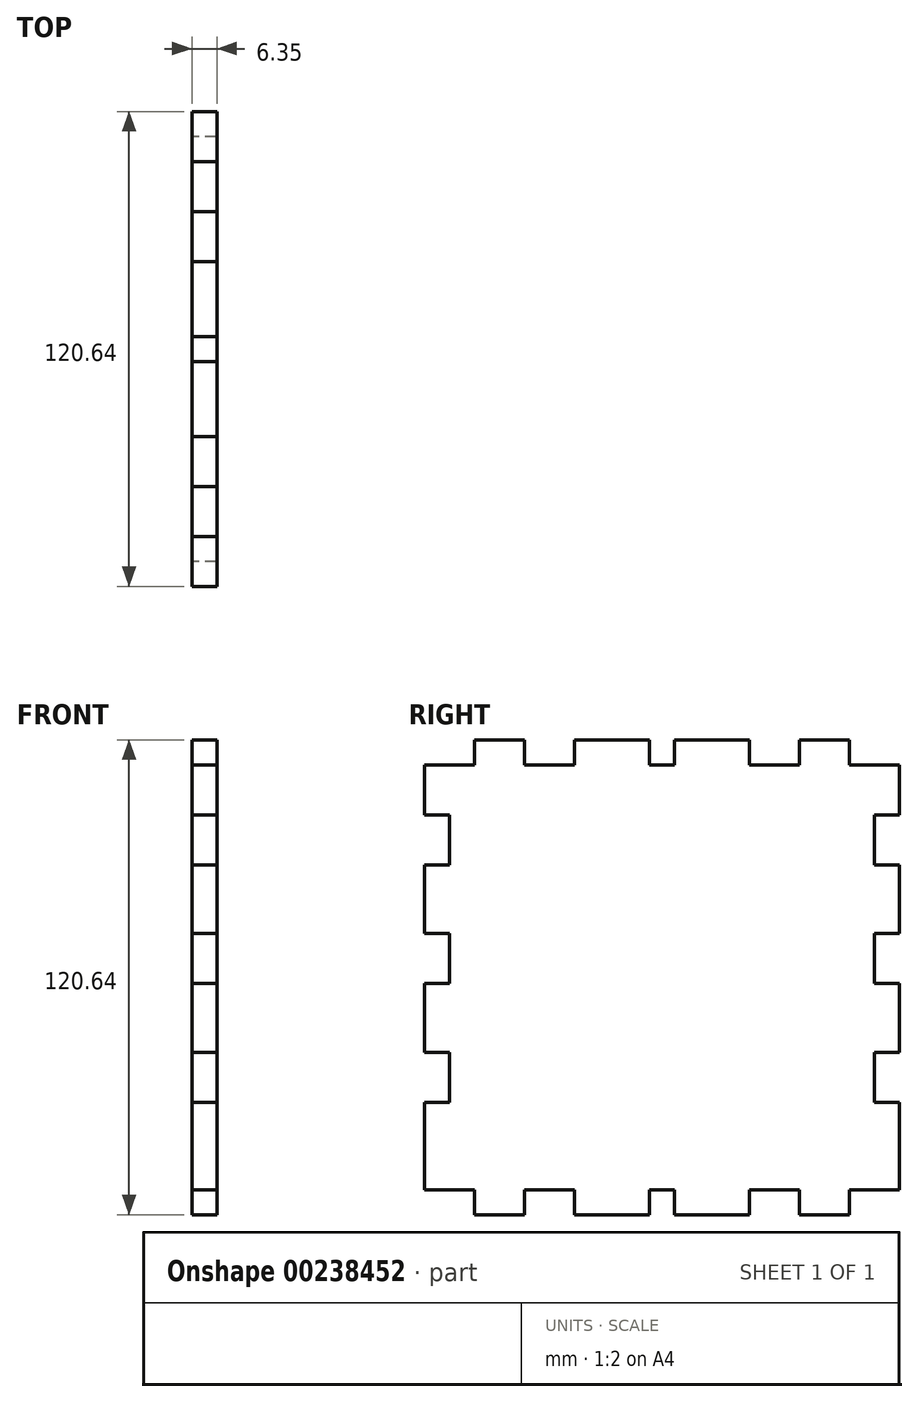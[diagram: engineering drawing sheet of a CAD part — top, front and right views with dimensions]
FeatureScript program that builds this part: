
annotation { "Feature Type Name" : "Feature", "Feature Type Description" : "" }
export const myFeature = defineFeature(function(context is Context, id is Id, definition is map)
    precondition{}
    {
        {
            var Q0;
            Q0=qCreatedBy(makeId("Right.planeOp"),FACE);
            var sketch = newSketch(context, id + "F0", { "sketchPlane" : qUnion([Q0])});
            skLineSegment(sketch, "E0.bottom", {"start": v(60.32, 60.33) * mm, "end": v(-60.33, 60.33) * mm});
            skLineSegment(sketch, "E0.top", {"start": v(60.33, -60.33) * mm, "end": v(-60.32, -60.33) * mm});
            skLineSegment(sketch, "E0.left", {"start": v(60.32, 60.33) * mm, "end": v(60.33, -60.33) * mm});
            skLineSegment(sketch, "E0.right", {"start": v(-60.33, 60.33) * mm, "end": v(-60.32, -60.33) * mm});
            skPoint(sketch, "E0.middle", {"position": v(0, 0) * mm});
            skSolve(sketch);
        }
        {
            var Q0;
            Q0=makeQuery(id+"F0.imprint","IMPRINT",FACE,{"disambiguationData":[TD([[makeQuery(id+"F0.imprint","IMPRINT",EDGE,{"derivedFrom":sQuery(id+"F0.wireOp",EDGE,"E0.bottom")}),1.0]])]});
            extrude(context, id + "F1", {"entities" : qUnion([Q0]), "depth" : 6.35 * mm});
        }
        {
            var Q0;
            Q0=makeQuery(id+"F1.opExtrude","CAP_FACE",FACE,{"disambiguationData":[OSD([sQuery(id+"F0.wireOp",EDGE,"E0.bottom"),sQuery(id+"F0.wireOp",EDGE,"E0.top"),sQuery(id+"F0.wireOp",EDGE,"E0.left"),sQuery(id+"F0.wireOp",EDGE,"E0.right")])],"isStart":true});
            var sketch = newSketch(context, id + "F2", { "sketchPlane" : qUnion([Q0])});
            skLineSegment(sketch, "E1.bottom", {"start": v(60.33, 60.33) * mm, "end": v(47.63, 60.33) * mm});
            skLineSegment(sketch, "E1.top", {"start": v(60.33, 53.98) * mm, "end": v(47.63, 53.98) * mm});
            skLineSegment(sketch, "E1.left", {"start": v(60.33, 60.33) * mm, "end": v(60.33, 53.98) * mm});
            skLineSegment(sketch, "E1.right", {"start": v(47.63, 60.33) * mm, "end": v(47.63, 53.98) * mm});
            skSolve(sketch);
        }
        {
            var Q0;
            Q0=makeQuery(id+"F2.imprint","IMPRINT",FACE,{"disambiguationData":[TD([[makeQuery(id+"F2.imprint","IMPRINT",EDGE,{"derivedFrom":sQuery(id+"F2.wireOp",EDGE,"E1.bottom")}),-1.0]])]});
            extrude(context, id + "F3", {"entities" : qUnion([Q0]), "operationType" : NewBodyOperationType.REMOVE, "endBound" : BoundingType.THROUGH_ALL, "oppositeDirection" : true, "depth" : 1.59 * mm});
        }
        {
            var Q0;
            Q0=makeQuery(id+"F1.opExtrude","CAP_FACE",FACE,{"disambiguationData":[OSD([sQuery(id+"F0.wireOp",EDGE,"E0.bottom"),sQuery(id+"F0.wireOp",EDGE,"E0.top"),sQuery(id+"F0.wireOp",EDGE,"E0.left"),sQuery(id+"F0.wireOp",EDGE,"E0.right")])],"isStart":true});
            var sketch = newSketch(context, id + "F4", { "sketchPlane" : qUnion([Q0])});
            skLineSegment(sketch, "E2.bottom", {"start": v(34.93, 60.33) * mm, "end": v(22.23, 60.33) * mm});
            skLineSegment(sketch, "E2.top", {"start": v(34.93, 53.98) * mm, "end": v(22.23, 53.98) * mm});
            skLineSegment(sketch, "E2.left", {"start": v(34.93, 60.33) * mm, "end": v(34.93, 53.98) * mm});
            skLineSegment(sketch, "E2.right", {"start": v(22.23, 60.33) * mm, "end": v(22.23, 53.98) * mm});
            skSolve(sketch);
        }
        {
            var Q0;
            Q0=qSketchRegion(id+"F4",true);
            extrude(context, id + "F5", {"entities" : qUnion([Q0]), "operationType" : NewBodyOperationType.REMOVE, "endBound" : BoundingType.THROUGH_ALL, "oppositeDirection" : true, "depth" : 1.59 * mm});
        }
        {
            var Q0;
            Q0=makeQuery(id+"F1.opExtrude","CAP_FACE",FACE,{"disambiguationData":[OSD([sQuery(id+"F0.wireOp",EDGE,"E0.bottom"),sQuery(id+"F0.wireOp",EDGE,"E0.top"),sQuery(id+"F0.wireOp",EDGE,"E0.left"),sQuery(id+"F0.wireOp",EDGE,"E0.right")])],"isStart":true});
            var sketch = newSketch(context, id + "F6", { "sketchPlane" : qUnion([Q0])});
            skLineSegment(sketch, "E3.bottom", {"start": v(3.18, 60.33) * mm, "end": v(-3.17, 60.33) * mm});
            skLineSegment(sketch, "E3.top", {"start": v(3.18, 53.98) * mm, "end": v(-3.17, 53.98) * mm});
            skLineSegment(sketch, "E3.left", {"start": v(3.18, 60.33) * mm, "end": v(3.18, 53.98) * mm});
            skLineSegment(sketch, "E3.right", {"start": v(-3.17, 60.33) * mm, "end": v(-3.17, 53.98) * mm});
            skSolve(sketch);
        }
        {
            var Q0;
            Q0=qSketchRegion(id+"F6",true);
            extrude(context, id + "F7", {"entities" : qUnion([Q0]), "operationType" : NewBodyOperationType.REMOVE, "endBound" : BoundingType.THROUGH_ALL, "oppositeDirection" : true, "depth" : 1.59 * mm});
        }
        {
            var Q0;
            Q0=makeQuery(id+"F1.opExtrude","CAP_FACE",FACE,{"disambiguationData":[OSD([sQuery(id+"F0.wireOp",EDGE,"E0.bottom"),sQuery(id+"F0.wireOp",EDGE,"E0.top"),sQuery(id+"F0.wireOp",EDGE,"E0.left"),sQuery(id+"F0.wireOp",EDGE,"E0.right")])],"isStart":true});
            var sketch = newSketch(context, id + "F8", { "sketchPlane" : qUnion([Q0])});
            skLineSegment(sketch, "E4.bottom", {"start": v(-60.32, 60.33) * mm, "end": v(-47.62, 60.33) * mm});
            skLineSegment(sketch, "E4.top", {"start": v(-60.32, 53.98) * mm, "end": v(-47.62, 53.98) * mm});
            skLineSegment(sketch, "E4.left", {"start": v(-60.32, 60.33) * mm, "end": v(-60.32, 53.98) * mm});
            skLineSegment(sketch, "E4.right", {"start": v(-47.62, 60.33) * mm, "end": v(-47.62, 53.98) * mm});
            skSolve(sketch);
        }
        {
            var Q0;
            Q0=makeQuery(id+"F8.imprint","IMPRINT",FACE,{"disambiguationData":[TD([[makeQuery(id+"F8.imprint","IMPRINT",EDGE,{"derivedFrom":sQuery(id+"F8.wireOp",EDGE,"E4.bottom")}),-1.0]])]});
            extrude(context, id + "F9", {"entities" : qUnion([Q0]), "operationType" : NewBodyOperationType.REMOVE, "endBound" : BoundingType.THROUGH_ALL, "oppositeDirection" : true, "depth" : 1.59 * mm});
        }
        {
            var Q0;
            Q0=makeQuery(id+"F1.opExtrude","CAP_FACE",FACE,{"disambiguationData":[OSD([sQuery(id+"F0.wireOp",EDGE,"E0.bottom"),sQuery(id+"F0.wireOp",EDGE,"E0.top"),sQuery(id+"F0.wireOp",EDGE,"E0.left"),sQuery(id+"F0.wireOp",EDGE,"E0.right")])],"isStart":true});
            var sketch = newSketch(context, id + "F10", { "sketchPlane" : qUnion([Q0])});
            skLineSegment(sketch, "E5.bottom", {"start": v(-22.22, 60.33) * mm, "end": v(-34.92, 60.33) * mm});
            skLineSegment(sketch, "E5.top", {"start": v(-22.22, 53.98) * mm, "end": v(-34.92, 53.98) * mm});
            skLineSegment(sketch, "E5.left", {"start": v(-22.22, 60.33) * mm, "end": v(-22.22, 53.98) * mm});
            skLineSegment(sketch, "E5.right", {"start": v(-34.92, 60.33) * mm, "end": v(-34.92, 53.98) * mm});
            skSolve(sketch);
        }
        {
            var Q0;
            Q0=makeQuery(id+"F10.imprint","IMPRINT",FACE,{"disambiguationData":[TD([[makeQuery(id+"F10.imprint","IMPRINT",EDGE,{"derivedFrom":sQuery(id+"F10.wireOp",EDGE,"E5.bottom")}),-1.0]])]});
            extrude(context, id + "F11", {"entities" : qUnion([Q0]), "operationType" : NewBodyOperationType.REMOVE, "endBound" : BoundingType.THROUGH_ALL, "oppositeDirection" : true, "depth" : 1.59 * mm});
        }
        {
            var Q0;
            Q0=makeQuery(id+"F1.opExtrude","CAP_FACE",FACE,{"disambiguationData":[OSD([sQuery(id+"F0.wireOp",EDGE,"E0.bottom"),sQuery(id+"F0.wireOp",EDGE,"E0.top"),sQuery(id+"F0.wireOp",EDGE,"E0.left"),sQuery(id+"F0.wireOp",EDGE,"E0.right")])],"isStart":true});
            var sketch = newSketch(context, id + "F12", { "sketchPlane" : qUnion([Q0])});
            skLineSegment(sketch, "E6.bottom", {"start": v(-60.32, 41.28) * mm, "end": v(-53.97, 41.28) * mm});
            skLineSegment(sketch, "E6.top", {"start": v(-60.32, 28.58) * mm, "end": v(-53.97, 28.58) * mm});
            skLineSegment(sketch, "E6.left", {"start": v(-60.32, 41.28) * mm, "end": v(-60.32, 28.57) * mm});
            skLineSegment(sketch, "E6.right", {"start": v(-53.97, 41.28) * mm, "end": v(-53.97, 28.58) * mm});
            skSolve(sketch);
        }
        {
            var Q0;
            Q0=makeQuery(id+"F12.imprint","IMPRINT",FACE,{"disambiguationData":[TD([[makeQuery(id+"F12.imprint","IMPRINT",EDGE,{"derivedFrom":sQuery(id+"F12.wireOp",EDGE,"E6.bottom")}),-1.0]])]});
            extrude(context, id + "F13", {"entities" : qUnion([Q0]), "operationType" : NewBodyOperationType.REMOVE, "endBound" : BoundingType.THROUGH_ALL, "oppositeDirection" : true, "depth" : 1.59 * mm});
        }
        {
            var Q0;
            Q0=makeQuery(id+"F1.opExtrude","CAP_FACE",FACE,{"disambiguationData":[OSD([sQuery(id+"F0.wireOp",EDGE,"E0.bottom"),sQuery(id+"F0.wireOp",EDGE,"E0.top"),sQuery(id+"F0.wireOp",EDGE,"E0.left"),sQuery(id+"F0.wireOp",EDGE,"E0.right")])],"isStart":true});
            var sketch = newSketch(context, id + "F14", { "sketchPlane" : qUnion([Q0])});
            skLineSegment(sketch, "E7.bottom", {"start": v(-60.32, 11.11) * mm, "end": v(-53.97, 11.11) * mm});
            skLineSegment(sketch, "E7.top", {"start": v(-60.32, -1.59) * mm, "end": v(-53.97, -1.59) * mm});
            skLineSegment(sketch, "E7.left", {"start": v(-60.32, 11.11) * mm, "end": v(-60.32, -1.59) * mm});
            skLineSegment(sketch, "E7.right", {"start": v(-53.97, 11.11) * mm, "end": v(-53.97, -1.59) * mm});
            skSolve(sketch);
        }
        {
            var Q0;
            Q0=makeQuery(id+"F14.imprint","IMPRINT",FACE,{"disambiguationData":[TD([[makeQuery(id+"F14.imprint","IMPRINT",EDGE,{"derivedFrom":sQuery(id+"F14.wireOp",EDGE,"E7.bottom")}),-1.0]])]});
            extrude(context, id + "F15", {"entities" : qUnion([Q0]), "operationType" : NewBodyOperationType.REMOVE, "endBound" : BoundingType.THROUGH_ALL, "oppositeDirection" : true, "depth" : 1.59 * mm});
        }
        {
            var Q0;
            Q0=makeQuery(id+"F1.opExtrude","CAP_FACE",FACE,{"disambiguationData":[OSD([sQuery(id+"F0.wireOp",EDGE,"E0.bottom"),sQuery(id+"F0.wireOp",EDGE,"E0.top"),sQuery(id+"F0.wireOp",EDGE,"E0.left"),sQuery(id+"F0.wireOp",EDGE,"E0.right")])],"isStart":true});
            var sketch = newSketch(context, id + "F16", { "sketchPlane" : qUnion([Q0])});
            skLineSegment(sketch, "E8.bottom", {"start": v(-60.33, -19.05) * mm, "end": v(-53.98, -19.05) * mm});
            skLineSegment(sketch, "E8.top", {"start": v(-60.33, -31.75) * mm, "end": v(-53.98, -31.75) * mm});
            skLineSegment(sketch, "E8.left", {"start": v(-60.33, -19.05) * mm, "end": v(-60.33, -31.75) * mm});
            skLineSegment(sketch, "E8.right", {"start": v(-53.98, -19.05) * mm, "end": v(-53.98, -31.75) * mm});
            skSolve(sketch);
        }
        {
            var Q0;
            Q0=makeQuery(id+"F16.imprint","IMPRINT",FACE,{"disambiguationData":[TD([[makeQuery(id+"F16.imprint","IMPRINT",EDGE,{"derivedFrom":sQuery(id+"F16.wireOp",EDGE,"E8.bottom")}),-1.0]])]});
            extrude(context, id + "F17", {"entities" : qUnion([Q0]), "operationType" : NewBodyOperationType.REMOVE, "endBound" : BoundingType.THROUGH_ALL, "oppositeDirection" : true, "depth" : 1.59 * mm});
        }
        {
            var Q0;
            Q0=makeQuery(id+"F1.opExtrude","CAP_FACE",FACE,{"disambiguationData":[OSD([sQuery(id+"F0.wireOp",EDGE,"E0.bottom"),sQuery(id+"F0.wireOp",EDGE,"E0.top"),sQuery(id+"F0.wireOp",EDGE,"E0.left"),sQuery(id+"F0.wireOp",EDGE,"E0.right")])],"isStart":true});
            var sketch = newSketch(context, id + "F18", { "sketchPlane" : qUnion([Q0])});
            skLineSegment(sketch, "E9.bottom", {"start": v(-60.33, -53.98) * mm, "end": v(-47.63, -53.98) * mm});
            skLineSegment(sketch, "E9.top", {"start": v(-60.33, -60.33) * mm, "end": v(-47.63, -60.33) * mm});
            skLineSegment(sketch, "E9.left", {"start": v(-60.33, -53.98) * mm, "end": v(-60.33, -60.33) * mm});
            skLineSegment(sketch, "E9.right", {"start": v(-47.63, -53.98) * mm, "end": v(-47.63, -60.33) * mm});
            skLineSegment(sketch, "E10.bottom", {"start": v(60.32, -53.98) * mm, "end": v(47.62, -53.98) * mm});
            skLineSegment(sketch, "E10.top", {"start": v(60.32, -60.33) * mm, "end": v(47.62, -60.33) * mm});
            skLineSegment(sketch, "E10.left", {"start": v(60.32, -53.98) * mm, "end": v(60.32, -60.33) * mm});
            skLineSegment(sketch, "E10.right", {"start": v(47.62, -53.98) * mm, "end": v(47.62, -60.33) * mm});
            skSolve(sketch);
        }
        {
            var Q0;
            Q0=qSketchRegion(id+"F18",true);
            extrude(context, id + "F19", {"entities" : qUnion([Q0]), "operationType" : NewBodyOperationType.REMOVE, "endBound" : BoundingType.THROUGH_ALL, "oppositeDirection" : true, "depth" : 1.59 * mm});
        }
        {
            var Q0;
            Q0=makeQuery(id+"F1.opExtrude","CAP_FACE",FACE,{"disambiguationData":[OSD([sQuery(id+"F0.wireOp",EDGE,"E0.bottom"),sQuery(id+"F0.wireOp",EDGE,"E0.top"),sQuery(id+"F0.wireOp",EDGE,"E0.left"),sQuery(id+"F0.wireOp",EDGE,"E0.right")])],"isStart":true});
            var sketch = newSketch(context, id + "F20", { "sketchPlane" : qUnion([Q0])});
            skLineSegment(sketch, "E11.bottom", {"start": v(-34.93, -60.33) * mm, "end": v(-22.23, -60.33) * mm});
            skLineSegment(sketch, "E11.top", {"start": v(-34.93, -53.98) * mm, "end": v(-22.23, -53.98) * mm});
            skLineSegment(sketch, "E11.left", {"start": v(-34.93, -60.33) * mm, "end": v(-34.93, -53.98) * mm});
            skLineSegment(sketch, "E11.right", {"start": v(-22.23, -60.33) * mm, "end": v(-22.23, -53.98) * mm});
            skLineSegment(sketch, "E12.bottom", {"start": v(-3.18, -60.33) * mm, "end": v(3.17, -60.33) * mm});
            skLineSegment(sketch, "E12.top", {"start": v(-3.18, -53.98) * mm, "end": v(3.17, -53.98) * mm});
            skLineSegment(sketch, "E12.left", {"start": v(-3.18, -60.33) * mm, "end": v(-3.18, -53.98) * mm});
            skLineSegment(sketch, "E12.right", {"start": v(3.17, -60.33) * mm, "end": v(3.17, -53.98) * mm});
            skLineSegment(sketch, "E13.bottom", {"start": v(22.22, -60.33) * mm, "end": v(34.92, -60.33) * mm});
            skLineSegment(sketch, "E13.top", {"start": v(22.22, -53.97) * mm, "end": v(34.92, -53.97) * mm});
            skLineSegment(sketch, "E13.left", {"start": v(22.22, -60.33) * mm, "end": v(22.22, -53.97) * mm});
            skLineSegment(sketch, "E13.right", {"start": v(34.92, -60.33) * mm, "end": v(34.92, -53.97) * mm});
            skSolve(sketch);
        }
        {
            var Q0;
            Q0=qSketchRegion(id+"F20",true);
            extrude(context, id + "F21", {"entities" : qUnion([Q0]), "operationType" : NewBodyOperationType.REMOVE, "endBound" : BoundingType.THROUGH_ALL, "oppositeDirection" : true, "depth" : 1.59 * mm});
        }
        {
            var Q0;
            Q0=makeQuery(id+"F1.opExtrude","CAP_FACE",FACE,{"disambiguationData":[OSD([sQuery(id+"F0.wireOp",EDGE,"E0.bottom"),sQuery(id+"F0.wireOp",EDGE,"E0.top"),sQuery(id+"F0.wireOp",EDGE,"E0.left"),sQuery(id+"F0.wireOp",EDGE,"E0.right")])],"isStart":true});
            var sketch = newSketch(context, id + "F22", { "sketchPlane" : qUnion([Q0])});
            skLineSegment(sketch, "E14.bottom", {"start": v(60.33, 41.27) * mm, "end": v(53.98, 41.27) * mm});
            skLineSegment(sketch, "E14.top", {"start": v(60.33, 28.57) * mm, "end": v(53.98, 28.57) * mm});
            skLineSegment(sketch, "E14.left", {"start": v(60.33, 41.27) * mm, "end": v(60.33, 28.57) * mm});
            skLineSegment(sketch, "E14.right", {"start": v(53.98, 41.27) * mm, "end": v(53.98, 28.57) * mm});
            skLineSegment(sketch, "E15.bottom", {"start": v(60.33, 11.11) * mm, "end": v(53.98, 11.11) * mm});
            skLineSegment(sketch, "E15.top", {"start": v(60.33, -1.59) * mm, "end": v(53.98, -1.59) * mm});
            skLineSegment(sketch, "E15.left", {"start": v(60.33, 11.11) * mm, "end": v(60.33, -1.59) * mm});
            skLineSegment(sketch, "E15.right", {"start": v(53.98, 11.11) * mm, "end": v(53.98, -1.59) * mm});
            skSolve(sketch);
        }
        {
            var Q0;
            Q0=qSketchRegion(id+"F22",true);
            extrude(context, id + "F23", {"entities" : qUnion([Q0]), "operationType" : NewBodyOperationType.REMOVE, "endBound" : BoundingType.THROUGH_ALL, "oppositeDirection" : true, "depth" : 1.59 * mm});
        }
        {
            var Q0;
            Q0=makeQuery(id+"F1.opExtrude","CAP_FACE",FACE,{"disambiguationData":[OSD([sQuery(id+"F0.wireOp",EDGE,"E0.bottom"),sQuery(id+"F0.wireOp",EDGE,"E0.top"),sQuery(id+"F0.wireOp",EDGE,"E0.left"),sQuery(id+"F0.wireOp",EDGE,"E0.right")])],"isStart":true});
            var sketch = newSketch(context, id + "F24", { "sketchPlane" : qUnion([Q0])});
            skLineSegment(sketch, "E16.bottom", {"start": v(60.33, -19.05) * mm, "end": v(53.98, -19.05) * mm});
            skLineSegment(sketch, "E16.top", {"start": v(60.33, -31.75) * mm, "end": v(53.98, -31.75) * mm});
            skLineSegment(sketch, "E16.left", {"start": v(60.33, -19.05) * mm, "end": v(60.33, -31.75) * mm});
            skLineSegment(sketch, "E16.right", {"start": v(53.98, -19.05) * mm, "end": v(53.98, -31.75) * mm});
            skSolve(sketch);
        }
        {
            var Q0;
            Q0=qSketchRegion(id+"F24",true);
            extrude(context, id + "F25", {"entities" : qUnion([Q0]), "operationType" : NewBodyOperationType.REMOVE, "endBound" : BoundingType.THROUGH_ALL, "oppositeDirection" : true, "depth" : 1.59 * mm});
        }
    });
